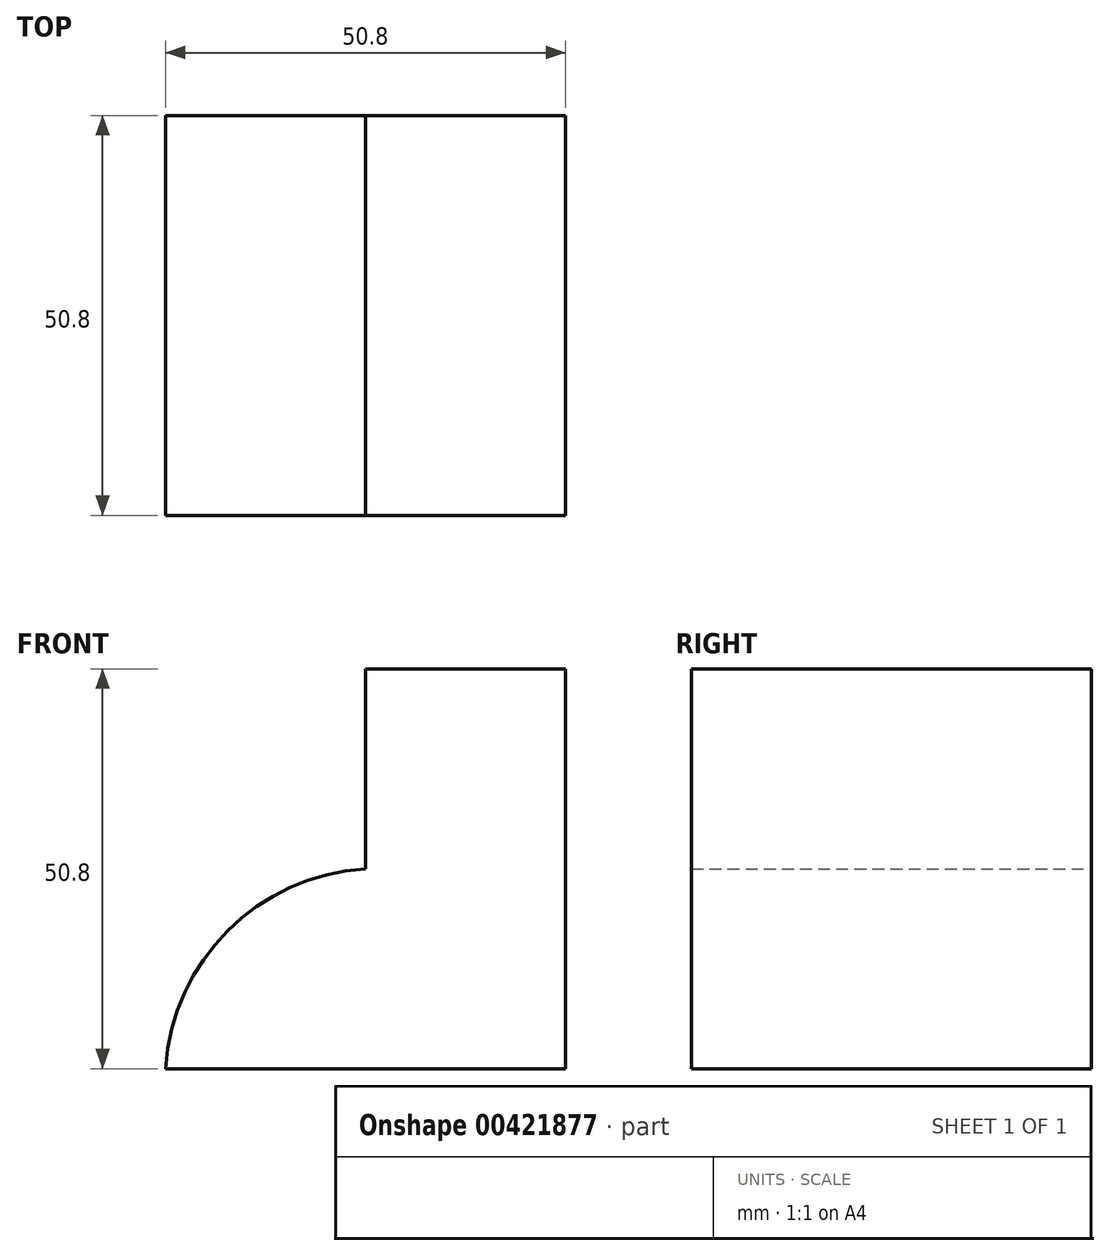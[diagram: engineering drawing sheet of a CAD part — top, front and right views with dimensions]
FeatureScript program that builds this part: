
annotation { "Feature Type Name" : "Feature", "Feature Type Description" : "" }
export const myFeature = defineFeature(function(context is Context, id is Id, definition is map)
    precondition{}
    {
        {
            var Q0;
            Q0=qCreatedBy(makeId("Front.planeOp"),FACE);
            var sketch = newSketch(context, id + "F0", { "sketchPlane" : qUnion([Q0])});
            skLineSegment(sketch, "E0", {"start": v(0, 0) * mm, "end": v(0, 50.8) * mm});
            skLineSegment(sketch, "E1", {"start": v(0, 50.8) * mm, "end": v(-25.4, 50.8) * mm});
            skLineSegment(sketch, "E2", {"start": v(-25.4, 50.8) * mm, "end": v(-25.4, 25.4) * mm});
            skLineSegment(sketch, "E3", {"start": v(0, 0) * mm, "end": v(-50.8, 0) * mm});
            skArc(sketch, "E4", {"start": v(-25.4, 25.4) * mm, "mid": v(-42.9, 17.5) * mm, "end": v(-50.8, 0) * mm});
            skSolve(sketch);
        }
        {
            var Q0;
            Q0 = qSketchRegion(id + "F0", true);
            extrude(context, id + "F1", {"entities" : qUnion([Q0]), "depth" : 50.8 * mm});
        }
    });
